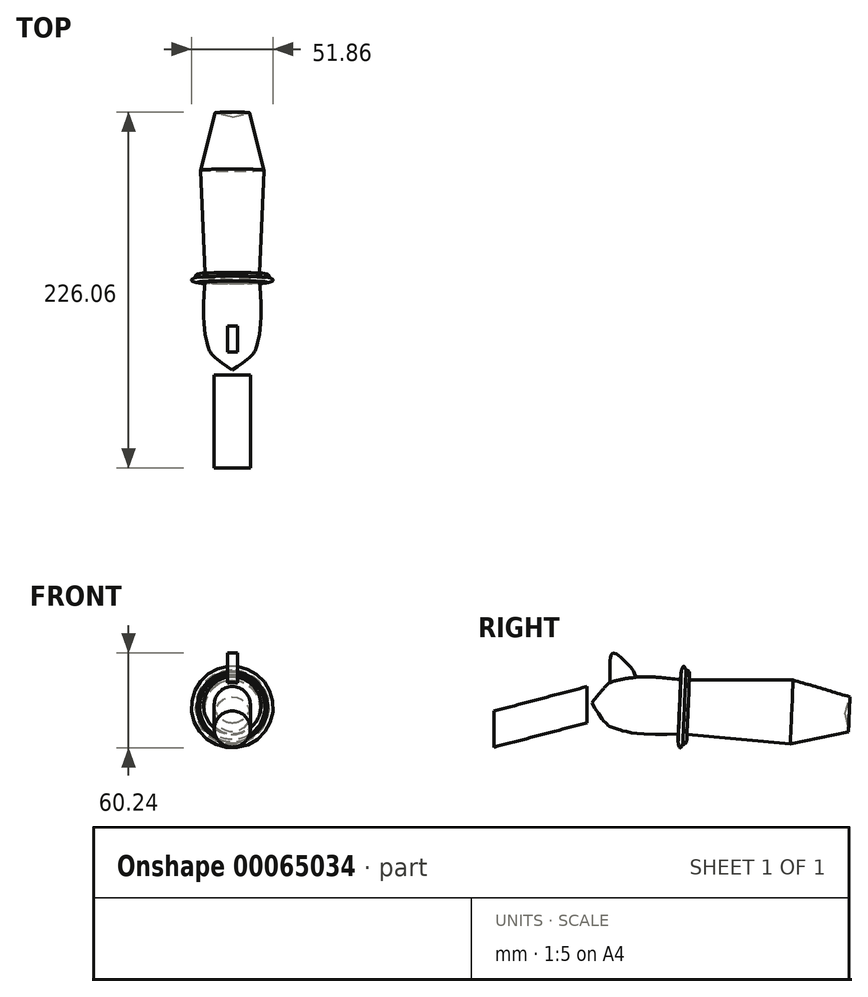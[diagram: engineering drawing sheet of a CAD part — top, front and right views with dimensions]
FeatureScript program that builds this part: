
annotation { "Feature Type Name" : "Feature", "Feature Type Description" : "" }
export const myFeature = defineFeature(function(context is Context, id is Id, definition is map)
    precondition{}
    {
        {
            var Q0;
            Q0=qCreatedBy(makeId("Right.planeOp"),FACE);
            var sketch = newSketch(context, id + "F0", { "sketchPlane" : qUnion([Q0])});
            skPoint(sketch, "E0.start.orphan", {"position": v(-138.82, 0) * mm});
            skLineSegment(sketch, "E1", {"start": v(-34.57, 0) * mm, "end": v(32.05, 0) * mm});
            skFitSpline(sketch, "E2", {"points": [v(-34.57, 0) * mm, v(-34.57, 5.95) * mm, v(-35.84, 3.68) * mm], "startDerivative": vector(5.43, 14.12) * mm, "endDerivative": vector(7.23, -21.7) * mm});
            skPoint(sketch, "E3.center.orphan", {"position": v(-39.02, 0) * mm});
            skLineSegment(sketch, "E4", {"start": v(-34.57, 0) * mm, "end": v(-39.02, 0) * mm});
            skLineSegment(sketch, "E5", {"start": v(-39.02, 3.6) * mm, "end": v(-39.02, 0) * mm});
            skLineSegment(sketch, "E6", {"start": v(-35.84, 3.68) * mm, "end": v(-35.84, 0) * mm});
            skPoint(sketch, "E6.endSnap0", {"position": v(-36.8, 0) * mm});
            skFitSpline(sketch, "E7", {"points": [v(-39.02, 3.6) * mm, v(-37.42, 8.74) * mm, v(-35.84, 3.68) * mm], "startDerivative": vector(-2, 6.84) * mm, "endDerivative": vector(-1.9, -4.85) * mm});
            skFitSpline(sketch, "E8", {"points": [v(-39.02, 3.6) * mm, v(-38.3, 5.32) * mm], "startDerivative": vector(-1.99, 2.42) * mm, "endDerivative": vector(0.57, -3.97) * mm});
            skPoint(sketch, "E9.end.orphan", {"position": v(-38.5, 6.88) * mm});
            skLineSegment(sketch, "E10", {"start": v(-38.3, 5.32) * mm, "end": v(-38.3, 4.5) * mm});
            skLineSegment(sketch, "E11", {"start": v(-38.3, 4.5) * mm, "end": v(-38.3, 0) * mm});
            skLineSegment(sketch, "E12", {"start": v(-39.02, 0) * mm, "end": v(-38.3, 0) * mm});
            skFitSpline(sketch, "E13", {"points": [v(-38.3, 0) * mm, v(-79.74, 0) * mm, v(-95.8, -14.68) * mm], "startDerivative": vector(-153.08, 21.3) * mm, "endDerivative": vector(-77.54, -104.78) * mm});
            skPoint(sketch, "E14.end.orphan", {"position": v(-84.94, -7.77) * mm});
            skLineSegment(sketch, "E15", {"start": v(32.05, 0) * mm, "end": v(68.15, -10.72) * mm});
            skLineSegment(sketch, "E16", {"start": v(68.15, -10.72) * mm, "end": v(64.9, -21.7) * mm});
            skLineSegment(sketch, "E17", {"start": v(64.9, -21.7) * mm, "end": v(-95.8, -14.68) * mm});
            skSolve(sketch);
        }
        {
            var Q0;
            Q0 = qSketchRegion(id + "F0", true);
            var Q1;
            Q1=sQuery(id+"F0.wireOp",EDGE,"E17");
            revolve(context, id + "F1", {"entities" : qUnion([Q0]), "axis" : qUnion([Q1]), "revolveType" : RevolveType.FULL});
        }
        {
            var Q0;
            Q0=qCreatedBy(makeId("Right.planeOp"),FACE);
            var sketch = newSketch(context, id + "F2", { "sketchPlane" : qUnion([Q0])});
            skFitSpline(sketch, "E18", {"points": [v(-67, 0) * mm, v(-73.17, 10.23) * mm, v(-82.3, 17.14) * mm, v(-84.26, -4.31) * mm], "startDerivative": vector(-29.48, 77.4) * mm, "endDerivative": vector(-1.31, -80.04) * mm});
            skLineSegment(sketch, "E19", {"start": v(-82.54, -4.31) * mm, "end": v(-67, 0) * mm});
            skLineSegment(sketch, "E20", {"start": v(-82.54, -4.31) * mm, "end": v(-84.26, -4.31) * mm});
            skSolve(sketch);
        }
        {
            var Q0;
            Q0 = qSketchRegion(id + "F2", true);
            extrude(context, id + "F3", {"entities" : qUnion([Q0]), "operationType" : NewBodyOperationType.ADD, "depth" : 3.19 * mm, "hasSecondDirection" : true, "secondDirectionOppositeDirection" : true, "secondDirectionDepth" : 2.87 * mm});
        }
        {
            var Q0;
            Q0=qCreatedBy(makeId("Front.planeOp"),FACE);
            cPlane(context, id + "F4", {"entities" : qUnion([Q0]), "cplaneType" : CPlaneType.OFFSET, "offset" : 98.8 * mm, "width" : 152.4 * mm, "height" : 152.4 * mm});
        }
        {
            var Q0;
            Q0=qCreatedBy(id+"F4.planeOp",FACE);
            var sketch = newSketch(context, id + "F5", { "sketchPlane" : qUnion([Q0])});
            skCircle(sketch, "E21", {"center": v(0, -15.66) * mm, "radius": 11.48 * mm});
            skSolve(sketch);
        }
        {
            var Q0;
            Q0=qCreatedBy(makeId("Right.planeOp"),FACE);
            var sketch = newSketch(context, id + "F6", { "sketchPlane" : qUnion([Q0])});
            skLineSegment(sketch, "E22", {"start": v(-98.97, -15.7) * mm, "end": v(-158.08, -31.2) * mm});
            skSolve(sketch);
        }
        {
            var Q0;
            Q0=makeQuery(id+"F5.imprint","IMPRINT",FACE,{"disambiguationData":[TD([[makeQuery(id+"F5.imprint","IMPRINT",EDGE,{"derivedFrom":sQuery(id+"F5.wireOp",EDGE,"E21")}),1.0]])]});
            var Q1;
            Q1=sQuery(id+"F6.wireOp",EDGE,"E22");
            sweep(context, id + "F7", {"profiles" : qUnion([Q0]), "path" : qUnion([Q1])});
        }
    });
